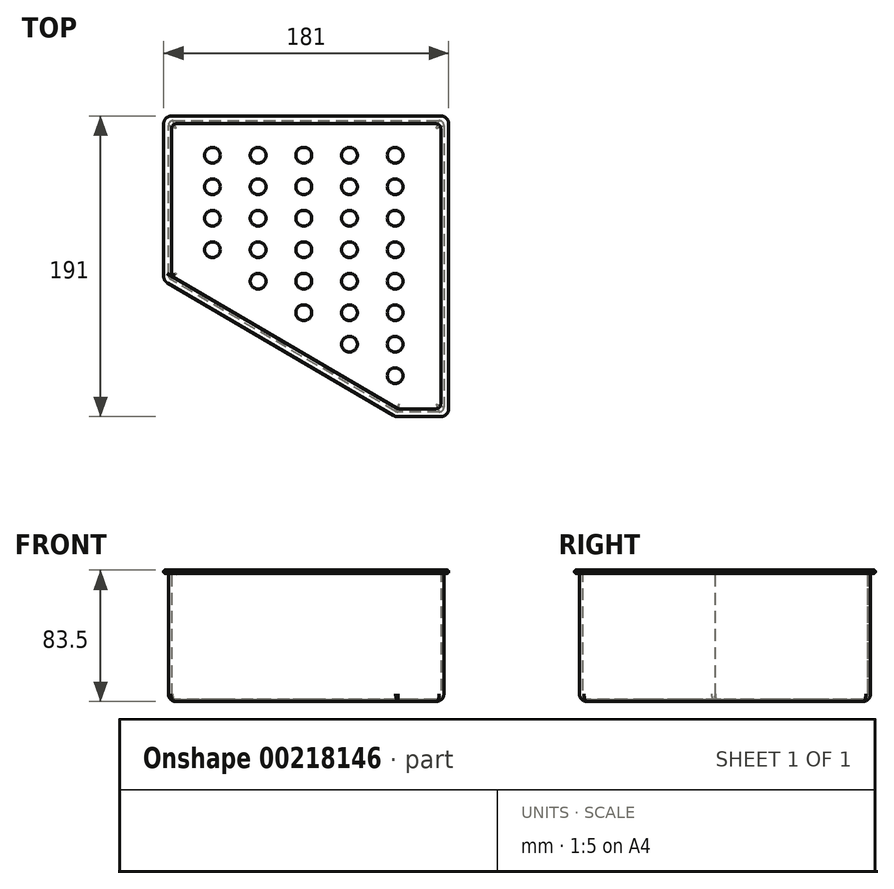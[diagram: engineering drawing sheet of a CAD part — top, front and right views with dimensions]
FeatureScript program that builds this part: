
annotation { "Feature Type Name" : "Feature", "Feature Type Description" : "" }
export const myFeature = defineFeature(function(context is Context, id is Id, definition is map)
    precondition{}
    {
        {
            var Q0;
            Q0=qCreatedBy(makeId("Top.planeOp"),FACE);
            var sketch = newSketch(context, id + "F0", { "sketchPlane" : qUnion([Q0])});
            skLineSegment(sketch, "E0", {"start": v(-87.5, 92.5) * mm, "end": v(87.5, 92.5) * mm});
            skLineSegment(sketch, "E1", {"start": v(87.5, 92.5) * mm, "end": v(87.5, -92.5) * mm});
            skLineSegment(sketch, "E2", {"start": v(87.5, -92.5) * mm, "end": v(57.5, -92.5) * mm});
            skLineSegment(sketch, "E3", {"start": v(57.5, -92.5) * mm, "end": v(-87.5, -7.5) * mm});
            skLineSegment(sketch, "E4", {"start": v(-87.5, -7.5) * mm, "end": v(-87.5, 92.5) * mm});
            skSolve(sketch);
        }
        {
            var Q0;
            Q0 = qSketchRegion(id + "F0", true);
            extrude(context, id + "F1", {"entities" : qUnion([Q0]), "depth" : 1.5 * mm});
        }
        {
            var Q0;
            Q0=makeQuery(id+"F1.opExtrude","CAP_FACE",FACE,{"disambiguationData":[OSD([sQuery(id+"F0.wireOp",EDGE,"E0"),sQuery(id+"F0.wireOp",EDGE,"E1"),sQuery(id+"F0.wireOp",EDGE,"E2"),sQuery(id+"F0.wireOp",EDGE,"E3"),sQuery(id+"F0.wireOp",EDGE,"E4")])],"isStart":false});
            var sketch = newSketch(context, id + "F2", { "sketchPlane" : qUnion([Q0])});
            skLineSegment(sketch, "E5", {"start": v(87.5, 92.5) * mm, "end": v(87.5, -92.5) * mm});
            skLineSegment(sketch, "E6", {"start": v(87.5, -92.5) * mm, "end": v(57.5, -92.5) * mm});
            skLineSegment(sketch, "E7", {"start": v(57.5, -92.5) * mm, "end": v(-87.5, -7.5) * mm});
            skLineSegment(sketch, "E8", {"start": v(-87.5, -7.5) * mm, "end": v(-87.5, 92.5) * mm});
            skLineSegment(sketch, "E9", {"start": v(-87.5, 92.5) * mm, "end": v(87.5, 92.5) * mm});
            skLineSegment(sketch, "E10.0", {"start": v(85.5, 90.5) * mm, "end": v(85.5, -90.5) * mm});
            skLineSegment(sketch, "E10.1", {"start": v(-85.5, 90.5) * mm, "end": v(85.5, 90.5) * mm});
            skLineSegment(sketch, "E10.2", {"start": v(85.5, -90.5) * mm, "end": v(58.04, -90.5) * mm});
            skLineSegment(sketch, "E10.3", {"start": v(58.04, -90.5) * mm, "end": v(-85.5, -6.35) * mm});
            skLineSegment(sketch, "E10.4", {"start": v(-85.5, -6.35) * mm, "end": v(-85.5, 90.5) * mm});
            skSolve(sketch);
        }
        {
            var Q0;
            Q0 = qSketchRegion(id + "F2", true);
            extrude(context, id + "F3", {"entities" : qUnion([Q0]), "operationType" : NewBodyOperationType.ADD, "depth" : 80 * mm});
        }
        {
            var Q0;
            Q0=makeQuery(id+"F3.opExtrude","CAP_FACE",FACE,{"disambiguationData":[OSD([sQuery(id+"F2.wireOp",EDGE,"E5"),sQuery(id+"F2.wireOp",EDGE,"E6"),sQuery(id+"F2.wireOp",EDGE,"E7"),sQuery(id+"F2.wireOp",EDGE,"E8"),sQuery(id+"F2.wireOp",EDGE,"E9"),sQuery(id+"F2.wireOp",EDGE,"E10.0"),sQuery(id+"F2.wireOp",EDGE,"E10.1"),sQuery(id+"F2.wireOp",EDGE,"E10.2"),sQuery(id+"F2.wireOp",EDGE,"E10.3"),sQuery(id+"F2.wireOp",EDGE,"E10.4")])],"isStart":false});
            var sketch = newSketch(context, id + "F4", { "sketchPlane" : qUnion([Q0])});
            skLineSegment(sketch, "E11", {"start": v(-85.5, 90.5) * mm, "end": v(85.5, 90.5) * mm});
            skLineSegment(sketch, "E12", {"start": v(85.5, 90.5) * mm, "end": v(85.5, -90.5) * mm});
            skLineSegment(sketch, "E13", {"start": v(85.5, -90.5) * mm, "end": v(58.04, -90.5) * mm});
            skLineSegment(sketch, "E14", {"start": v(58.04, -90.5) * mm, "end": v(-85.5, -6.35) * mm});
            skLineSegment(sketch, "E15", {"start": v(-85.5, -6.35) * mm, "end": v(-85.5, 90.5) * mm});
            skLineSegment(sketch, "E16.0", {"start": v(90.5, 95.5) * mm, "end": v(90.5, -95.5) * mm});
            skLineSegment(sketch, "E16.1", {"start": v(-90.5, 95.5) * mm, "end": v(90.5, 95.5) * mm});
            skLineSegment(sketch, "E16.2", {"start": v(90.5, -95.5) * mm, "end": v(56.69, -95.5) * mm});
            skLineSegment(sketch, "E16.3", {"start": v(56.69, -95.5) * mm, "end": v(-90.5, -9.22) * mm});
            skLineSegment(sketch, "E16.4", {"start": v(-90.5, -9.22) * mm, "end": v(-90.5, 95.5) * mm});
            skSolve(sketch);
        }
        {
            var Q0;
            Q0 = qSketchRegion(id + "F4", true);
            extrude(context, id + "F5", {"entities" : qUnion([Q0]), "operationType" : NewBodyOperationType.ADD, "depth" : 2 * mm});
        }
        {
            var Q0;
            Q0=makeQuery(id+"F1.opExtrude","CAP_FACE",FACE,{"disambiguationData":[OSD([sQuery(id+"F0.wireOp",EDGE,"E0"),sQuery(id+"F0.wireOp",EDGE,"E1"),sQuery(id+"F0.wireOp",EDGE,"E2"),sQuery(id+"F0.wireOp",EDGE,"E3"),sQuery(id+"F0.wireOp",EDGE,"E4")])],"isStart":false});
            var sketch = newSketch(context, id + "F6", { "sketchPlane" : qUnion([Q0])});
            skCircle(sketch, "E17", {"center": v(-59.5, 70.5) * mm, "radius": 5 * mm});
            skCircle(sketch, "E18", {"center": v(-59.5, 50.5) * mm, "radius": 5 * mm});
            skCircle(sketch, "E19", {"center": v(-59.5, 30.5) * mm, "radius": 5 * mm});
            skCircle(sketch, "E20", {"center": v(-59.5, 10.5) * mm, "radius": 5 * mm});
            skCircle(sketch, "E21", {"center": v(-30.5, 70.5) * mm, "radius": 5 * mm});
            skCircle(sketch, "E22", {"center": v(-30.5, 50.5) * mm, "radius": 5 * mm});
            skCircle(sketch, "E23", {"center": v(-30.5, 30.5) * mm, "radius": 5 * mm});
            skCircle(sketch, "E24", {"center": v(-30.5, 10.5) * mm, "radius": 5 * mm});
            skCircle(sketch, "E25", {"center": v(-30.5, -9.5) * mm, "radius": 5 * mm});
            skCircle(sketch, "E26", {"center": v(-1.5, 70.5) * mm, "radius": 5 * mm});
            skCircle(sketch, "E27", {"center": v(-1.5, 50.5) * mm, "radius": 5 * mm});
            skCircle(sketch, "E28", {"center": v(-1.5, 30.5) * mm, "radius": 5 * mm});
            skCircle(sketch, "E29", {"center": v(-1.5, 10.5) * mm, "radius": 5 * mm});
            skCircle(sketch, "E30", {"center": v(-1.5, -9.5) * mm, "radius": 5 * mm});
            skCircle(sketch, "E31", {"center": v(-1.5, -29.5) * mm, "radius": 5 * mm});
            skCircle(sketch, "E32", {"center": v(27.5, 70.5) * mm, "radius": 5 * mm});
            skCircle(sketch, "E33", {"center": v(27.5, 50.5) * mm, "radius": 5 * mm});
            skCircle(sketch, "E34", {"center": v(27.5, 30.5) * mm, "radius": 5 * mm});
            skCircle(sketch, "E35", {"center": v(27.5, 10.5) * mm, "radius": 5 * mm});
            skCircle(sketch, "E36", {"center": v(27.5, -9.5) * mm, "radius": 5 * mm});
            skCircle(sketch, "E37", {"center": v(27.5, -29.5) * mm, "radius": 5 * mm});
            skCircle(sketch, "E38", {"center": v(27.5, -49.5) * mm, "radius": 5 * mm});
            skCircle(sketch, "E39", {"center": v(56.5, 70.5) * mm, "radius": 5 * mm});
            skCircle(sketch, "E40", {"center": v(56.5, 50.5) * mm, "radius": 5 * mm});
            skCircle(sketch, "E41", {"center": v(56.5, 30.5) * mm, "radius": 5 * mm});
            skCircle(sketch, "E42", {"center": v(56.5, 10.5) * mm, "radius": 5 * mm});
            skCircle(sketch, "E43", {"center": v(56.5, -9.5) * mm, "radius": 5 * mm});
            skCircle(sketch, "E44", {"center": v(56.5, -29.5) * mm, "radius": 5 * mm});
            skCircle(sketch, "E45", {"center": v(56.5, -49.5) * mm, "radius": 5 * mm});
            skCircle(sketch, "E46", {"center": v(56.5, -69.5) * mm, "radius": 5 * mm});
            skSolve(sketch);
        }
        {
            var Q0;
            Q0 = qSketchRegion(id + "F6", true);
            extrude(context, id + "F7", {"entities" : qUnion([Q0]), "operationType" : NewBodyOperationType.REMOVE, "endBound" : BoundingType.THROUGH_ALL, "oppositeDirection" : true, "depth" : 25 * mm});
        }
        {
            var Q0;
            Q0=makeQuery(id+"F5.boolean.opBoolean","MERGE",EDGE,{"derivedFrom":[makeQuery(id+"F3.opExtrude","SWEPT_EDGE",EDGE,{"disambiguationData":[OSD([sQuery(id+"F2.wireOp",EDGE,"E10.1"),sQuery(id+"F2.wireOp",EDGE,"E10.4")])]}),makeQuery(id+"F5.opExtrude","SWEPT_EDGE",EDGE,{"disambiguationData":[OSD([sQuery(id+"F4.wireOp",EDGE,"E11"),sQuery(id+"F4.wireOp",EDGE,"E15")])]})]});
            var Q1;
            Q1=makeQuery(id+"F3.opExtrude","CAP_EDGE",EDGE,{"disambiguationData":[OSD([sQuery(id+"F2.wireOp",EDGE,"E10.1")])],"isStart":true});
            var Q2;
            Q2=makeQuery(id+"F3.opExtrude","CAP_EDGE",EDGE,{"disambiguationData":[OSD([sQuery(id+"F2.wireOp",EDGE,"E10.4")])],"isStart":true});
            var Q3;
            Q3=makeQuery(id+"F5.opExtrude","CAP_EDGE",EDGE,{"disambiguationData":[OSD([sQuery(id+"F4.wireOp",EDGE,"E15")])],"isStart":false});
            var Q4;
            Q4=makeQuery(id+"F5.boolean.opBoolean","MERGE",EDGE,{"derivedFrom":[makeQuery(id+"F3.opExtrude","SWEPT_EDGE",EDGE,{"disambiguationData":[OSD([sQuery(id+"F2.wireOp",EDGE,"E10.0"),sQuery(id+"F2.wireOp",EDGE,"E10.1")])]}),makeQuery(id+"F5.opExtrude","SWEPT_EDGE",EDGE,{"disambiguationData":[OSD([sQuery(id+"F4.wireOp",EDGE,"E11"),sQuery(id+"F4.wireOp",EDGE,"E12")])]})]});
            var Q5;
            Q5=makeQuery(id+"F3.opExtrude","CAP_EDGE",EDGE,{"disambiguationData":[OSD([sQuery(id+"F2.wireOp",EDGE,"E10.0")])],"isStart":true});
            var Q6;
            Q6=makeQuery(id+"F5.boolean.opBoolean","MERGE",EDGE,{"derivedFrom":[makeQuery(id+"F3.opExtrude","SWEPT_EDGE",EDGE,{"disambiguationData":[OSD([sQuery(id+"F2.wireOp",EDGE,"E10.0"),sQuery(id+"F2.wireOp",EDGE,"E10.2")])]}),makeQuery(id+"F5.opExtrude","SWEPT_EDGE",EDGE,{"disambiguationData":[OSD([sQuery(id+"F4.wireOp",EDGE,"E12"),sQuery(id+"F4.wireOp",EDGE,"E13")])]})]});
            var Q7;
            Q7=makeQuery(id+"F5.boolean.opBoolean","MERGE",EDGE,{"derivedFrom":[makeQuery(id+"F3.opExtrude","SWEPT_EDGE",EDGE,{"disambiguationData":[OSD([sQuery(id+"F2.wireOp",EDGE,"E10.2"),sQuery(id+"F2.wireOp",EDGE,"E10.3")])]}),makeQuery(id+"F5.opExtrude","SWEPT_EDGE",EDGE,{"disambiguationData":[OSD([sQuery(id+"F4.wireOp",EDGE,"E13"),sQuery(id+"F4.wireOp",EDGE,"E14")])]})]});
            var Q8;
            Q8=makeQuery(id+"F3.opExtrude","CAP_EDGE",EDGE,{"disambiguationData":[OSD([sQuery(id+"F2.wireOp",EDGE,"E10.3")])],"isStart":true});
            var Q9;
            Q9=makeQuery(id+"F3.opExtrude","CAP_EDGE",EDGE,{"disambiguationData":[OSD([sQuery(id+"F2.wireOp",EDGE,"E10.2")])],"isStart":true});
            var Q10;
            Q10=makeQuery(id+"F3.boolean.opBoolean","MERGE",EDGE,{"derivedFrom":[makeQuery(id+"F1.opExtrude","SWEPT_EDGE",EDGE,{"disambiguationData":[OSD([sQuery(id+"F0.wireOp",EDGE,"E3"),sQuery(id+"F0.wireOp",EDGE,"E4")])]}),makeQuery(id+"F3.opExtrude","SWEPT_EDGE",EDGE,{"disambiguationData":[OSD([sQuery(id+"F2.wireOp",EDGE,"E7"),sQuery(id+"F2.wireOp",EDGE,"E8")])]})]});
            var Q11;
            Q11=makeQuery(id+"F3.boolean.opBoolean","MERGE",EDGE,{"derivedFrom":[makeQuery(id+"F1.opExtrude","SWEPT_EDGE",EDGE,{"disambiguationData":[OSD([sQuery(id+"F0.wireOp",EDGE,"E0"),sQuery(id+"F0.wireOp",EDGE,"E4")])]}),makeQuery(id+"F3.opExtrude","SWEPT_EDGE",EDGE,{"disambiguationData":[OSD([sQuery(id+"F2.wireOp",EDGE,"E8"),sQuery(id+"F2.wireOp",EDGE,"E9")])]})]});
            var Q12;
            Q12=makeQuery(id+"F3.boolean.opBoolean","MERGE",EDGE,{"derivedFrom":[makeQuery(id+"F1.opExtrude","SWEPT_EDGE",EDGE,{"disambiguationData":[OSD([sQuery(id+"F0.wireOp",EDGE,"E0"),sQuery(id+"F0.wireOp",EDGE,"E1")])]}),makeQuery(id+"F3.opExtrude","SWEPT_EDGE",EDGE,{"disambiguationData":[OSD([sQuery(id+"F2.wireOp",EDGE,"E5"),sQuery(id+"F2.wireOp",EDGE,"E9")])]})]});
            var Q13;
            Q13=makeQuery(id+"F3.boolean.opBoolean","MERGE",EDGE,{"derivedFrom":[makeQuery(id+"F1.opExtrude","SWEPT_EDGE",EDGE,{"disambiguationData":[OSD([sQuery(id+"F0.wireOp",EDGE,"E1"),sQuery(id+"F0.wireOp",EDGE,"E2")])]}),makeQuery(id+"F3.opExtrude","SWEPT_EDGE",EDGE,{"disambiguationData":[OSD([sQuery(id+"F2.wireOp",EDGE,"E5"),sQuery(id+"F2.wireOp",EDGE,"E6")])]})]});
            var Q14;
            Q14=makeQuery(id+"F3.boolean.opBoolean","MERGE",EDGE,{"derivedFrom":[makeQuery(id+"F1.opExtrude","SWEPT_EDGE",EDGE,{"disambiguationData":[OSD([sQuery(id+"F0.wireOp",EDGE,"E2"),sQuery(id+"F0.wireOp",EDGE,"E3")])]}),makeQuery(id+"F3.opExtrude","SWEPT_EDGE",EDGE,{"disambiguationData":[OSD([sQuery(id+"F2.wireOp",EDGE,"E6"),sQuery(id+"F2.wireOp",EDGE,"E7")])]})]});
            fillet(context, id + "F8", {"entities" : qUnion([Q0, Q1, Q2, Q3, Q4, Q5, Q6, Q7, Q8, Q9, Q10, Q11, Q12, Q13, Q14]), "radius" : 3 * mm, "tangentPropagation" : true, "allowEdgeOverflow" : false});
        }
        {
            var Q0;
            Q0=makeQuery(id+"F5.opExtrude","SWEPT_EDGE",EDGE,{"disambiguationData":[OSD([sQuery(id+"F4.wireOp",EDGE,"E16.0"),sQuery(id+"F4.wireOp",EDGE,"E16.1")])]});
            var Q1;
            Q1=makeQuery(id+"F5.opExtrude","SWEPT_EDGE",EDGE,{"disambiguationData":[OSD([sQuery(id+"F4.wireOp",EDGE,"E16.1"),sQuery(id+"F4.wireOp",EDGE,"E16.4")])]});
            var Q2;
            Q2=makeQuery(id+"F5.opExtrude","SWEPT_EDGE",EDGE,{"disambiguationData":[OSD([sQuery(id+"F4.wireOp",EDGE,"E16.3"),sQuery(id+"F4.wireOp",EDGE,"E16.4")])]});
            var Q3;
            Q3=makeQuery(id+"F5.opExtrude","SWEPT_EDGE",EDGE,{"disambiguationData":[OSD([sQuery(id+"F4.wireOp",EDGE,"E16.2"),sQuery(id+"F4.wireOp",EDGE,"E16.3")])]});
            var Q4;
            Q4=makeQuery(id+"F5.opExtrude","SWEPT_EDGE",EDGE,{"disambiguationData":[OSD([sQuery(id+"F4.wireOp",EDGE,"E16.0"),sQuery(id+"F4.wireOp",EDGE,"E16.2")])]});
            fillet(context, id + "F9", {"entities" : qUnion([Q0, Q1, Q2, Q3, Q4]), "radius" : 5 * mm, "tangentPropagation" : true, "allowEdgeOverflow" : false});
        }
        {
            var Q0;
            Q0=makeQuery(id+"F5.opExtrude","CAP_EDGE",EDGE,{"disambiguationData":[OSD([sQuery(id+"F4.wireOp",EDGE,"E16.0")])],"isStart":false});
            var Q1;
            Q1=makeQuery(id+"F5.opExtrude","CAP_EDGE",EDGE,{"disambiguationData":[OSD([sQuery(id+"F4.wireOp",EDGE,"E16.1")])],"isStart":false});
            var Q2;
            Q2=makeQuery(id+"F5.opExtrude","CAP_EDGE",EDGE,{"disambiguationData":[OSD([sQuery(id+"F4.wireOp",EDGE,"E16.2")])],"isStart":false});
            var Q3;
            Q3=makeQuery(id+"F5.opExtrude","CAP_EDGE",EDGE,{"disambiguationData":[OSD([sQuery(id+"F4.wireOp",EDGE,"E16.3")])],"isStart":false});
            var Q4;
            Q4=makeQuery(id+"F5.opExtrude","CAP_EDGE",EDGE,{"disambiguationData":[OSD([sQuery(id+"F4.wireOp",EDGE,"E16.4")])],"isStart":false});
            var Q5;
            Q5=makeQuery(id+"F5.opExtrude","CAP_EDGE",EDGE,{"disambiguationData":[OSD([sQuery(id+"F4.wireOp",EDGE,"E16.1")])],"isStart":true});
            var Q6;
            Q6=makeQuery(id+"F5.opExtrude","CAP_EDGE",EDGE,{"disambiguationData":[OSD([sQuery(id+"F4.wireOp",EDGE,"E16.0")])],"isStart":true});
            var Q7;
            Q7=makeQuery(id+"F5.opExtrude","CAP_EDGE",EDGE,{"disambiguationData":[OSD([sQuery(id+"F4.wireOp",EDGE,"E16.2")])],"isStart":true});
            var Q8;
            Q8=makeQuery(id+"F5.opExtrude","CAP_EDGE",EDGE,{"disambiguationData":[OSD([sQuery(id+"F4.wireOp",EDGE,"E16.3")])],"isStart":true});
            var Q9;
            Q9=makeQuery(id+"F5.opExtrude","CAP_EDGE",EDGE,{"disambiguationData":[OSD([sQuery(id+"F4.wireOp",EDGE,"E16.4")])],"isStart":true});
            fillet(context, id + "F10", {"entities" : qUnion([Q0, Q1, Q2, Q3, Q4, Q5, Q6, Q7, Q8, Q9]), "radius" : 1 * mm, "tangentPropagation" : true, "allowEdgeOverflow" : false});
        }
        {
            var Q0;
            Q0=makeQuery(id+"F3.opExtrude","CAP_EDGE",EDGE,{"disambiguationData":[OSD([sQuery(id+"F2.wireOp",EDGE,"E8")])],"isStart":false});
            var Q1;
            Q1=makeQuery(id+"F1.opExtrude","CAP_EDGE",EDGE,{"disambiguationData":[OSD([sQuery(id+"F0.wireOp",EDGE,"E4")])],"isStart":true});
            fillet(context, id + "F11", {"entities" : qUnion([Q0, Q1]), "radius" : 5 * mm, "tangentPropagation" : true, "allowEdgeOverflow" : false});
        }
        {
            var Q0;
            Q0=makeQuery(id+"F1.opExtrude","CAP_FACE",FACE,{"disambiguationData":[OSD([sQuery(id+"F0.wireOp",EDGE,"E0"),sQuery(id+"F0.wireOp",EDGE,"E1"),sQuery(id+"F0.wireOp",EDGE,"E2"),sQuery(id+"F0.wireOp",EDGE,"E3"),sQuery(id+"F0.wireOp",EDGE,"E4")])],"isStart":false});
            fillet(context, id + "F12", {"entities" : qUnion([Q0]), "radius" : 2 * mm, "tangentPropagation" : true, "allowEdgeOverflow" : false});
        }
    });
